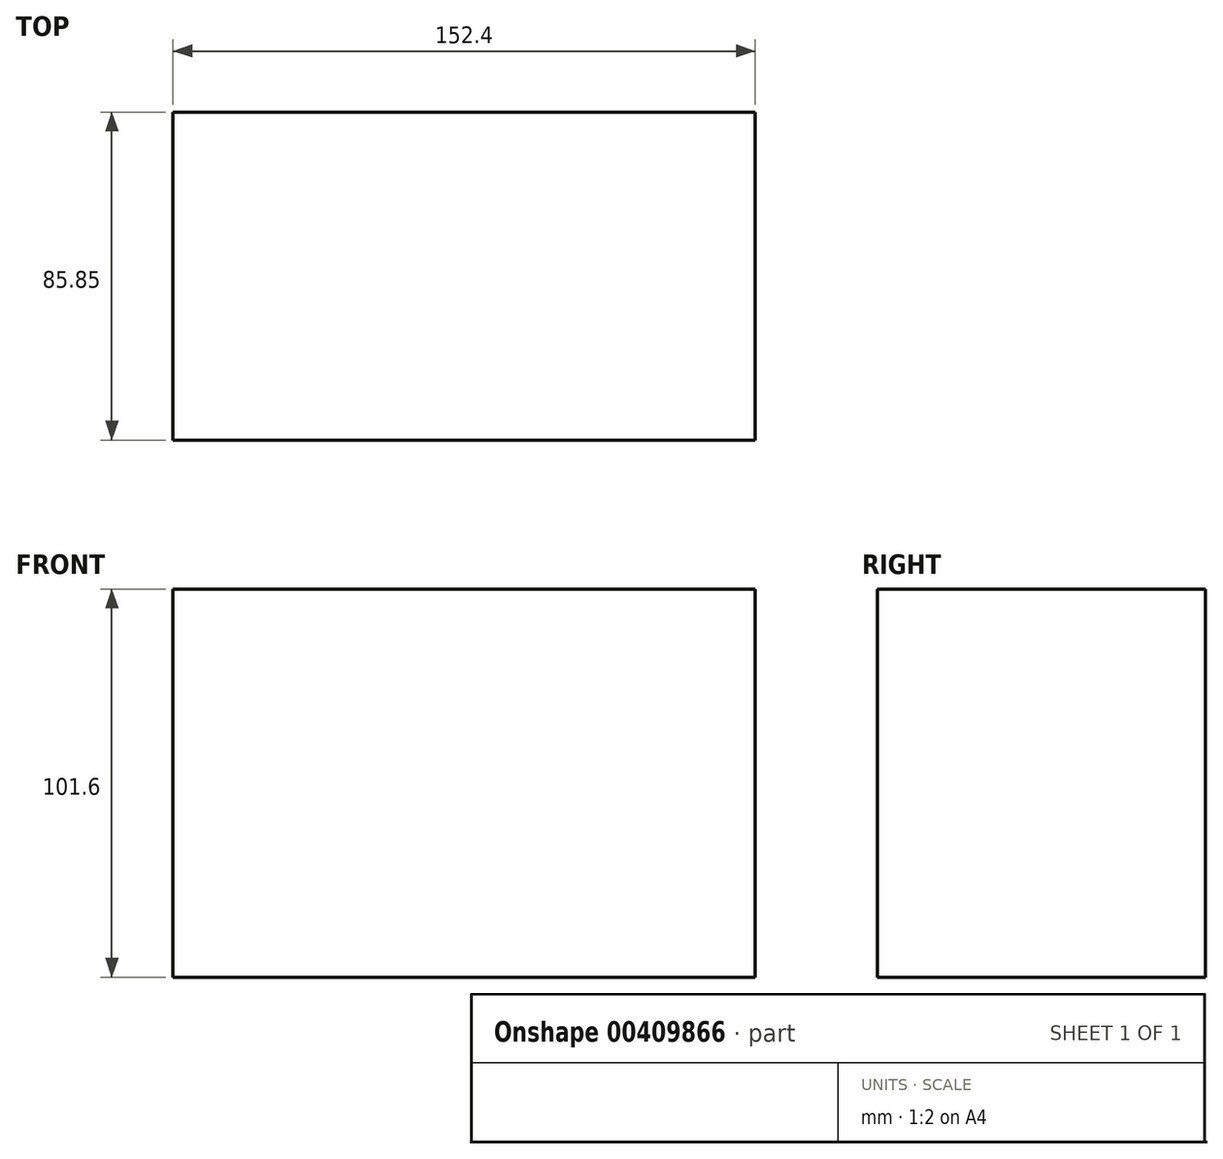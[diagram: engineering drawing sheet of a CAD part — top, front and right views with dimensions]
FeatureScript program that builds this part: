
annotation { "Feature Type Name" : "Feature", "Feature Type Description" : "" }
export const myFeature = defineFeature(function(context is Context, id is Id, definition is map)
    precondition{}
    {
        {
            var Q0;
            Q0=qCreatedBy(makeId("Front.planeOp"),FACE);
            var sketch = newSketch(context, id + "F0", { "sketchPlane" : qUnion([Q0])});
            skLineSegment(sketch, "E0", {"start": v(-76.2, 50.8) * mm, "end": v(-76.2, -50.8) * mm});
            skLineSegment(sketch, "E1", {"start": v(-76.2, -50.8) * mm, "end": v(76.2, -50.8) * mm});
            skLineSegment(sketch, "E2", {"start": v(76.2, -50.8) * mm, "end": v(76.2, 50.8) * mm});
            skLineSegment(sketch, "E3", {"start": v(76.2, 50.8) * mm, "end": v(-76.2, 50.8) * mm});
            skSolve(sketch);
        }
        {
            var Q0;
            Q0=makeQuery(id+"F0.imprint","IMPRINT",FACE,{"disambiguationData":[TD([[makeQuery(id+"F0.imprint","IMPRINT",EDGE,{"derivedFrom":sQuery(id+"F0.wireOp",EDGE,"E0")}),1.0]])]});
            extrude(context, id + "F1", {"entities" : qUnion([Q0]), "depth" : 85.85 * mm});
        }
    });
